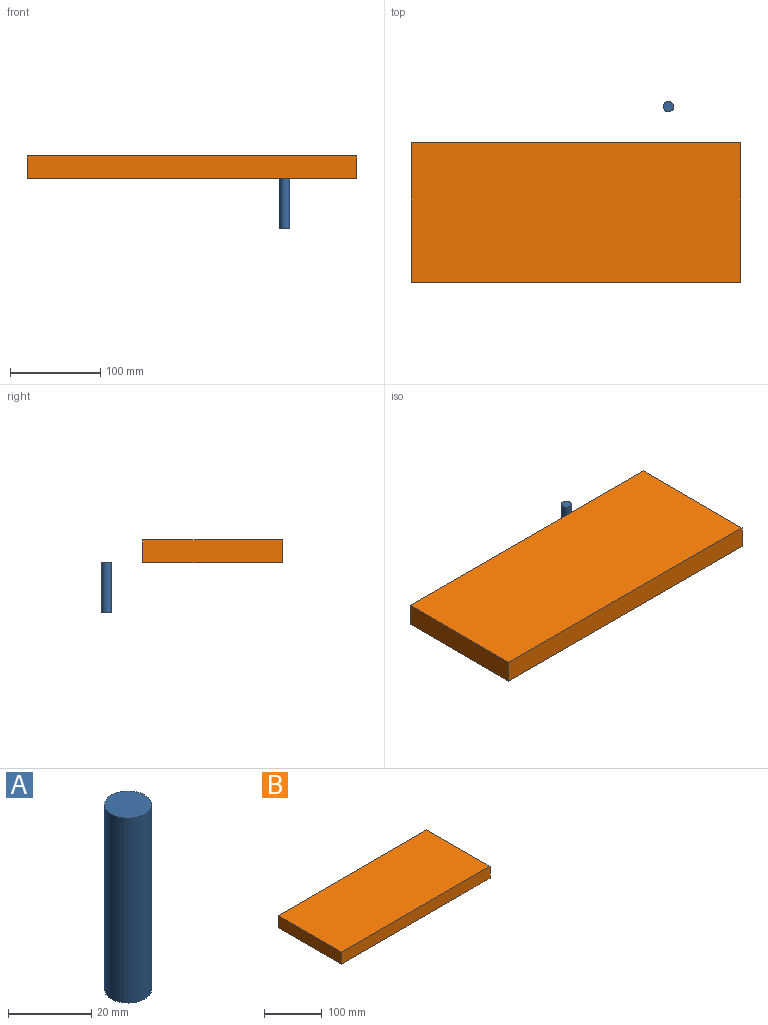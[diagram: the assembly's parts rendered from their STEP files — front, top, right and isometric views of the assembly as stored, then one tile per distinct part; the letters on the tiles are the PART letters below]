
ASSEMBLY  parts=2 mates=1
PART A: 3 faces, bbox 11.3x11.3x54.4 mm
  f0: cylinder r=5.66mm len=54.36mm, axis (0,0,-1), area 1934.7mm2, adj f1,f2
  f1: plane 11.33x11.33mm, normal (0,0,1), area 100.8mm2, adj f0
  f2: plane 11.33x11.33mm, normal (0,0,-1), area 100.8mm2, adj f0
PART B: 6 faces, bbox 364.5x154.8x25.4 mm
  f0: plane 154.82x25.4mm, normal (-1,0,0), area 3932.4mm2, adj f1,f3,f4,f5
  f1: plane 364.45x25.4mm, normal (0,-1,0), area 9257.1mm2, adj f0,f2,f4,f5
  f2: plane 154.82x25.4mm, normal (1,0,0), area 3932.4mm2, adj f1,f3,f4,f5
  f3: plane 364.45x25.4mm, normal (0,1,0), area 9257.1mm2, adj f0,f2,f4,f5
  f4: plane 364.45x154.82mm, normal (0,0,1), area 56423.8mm2, adj f0,f1,f2,f3
  f5: plane 364.45x154.82mm, normal (0,0,-1), area 56423.8mm2, adj f0,f1,f2,f3
PLACE A t=(4.05,-2.75,0.04)mm
PLACE B rot(axis=(0,-1,0),180deg) t=(8.37,-76.23,79.79)mm
MATE planar B.f4 <-> A.f0  axis (0,0,-1) through (-98.28,-120.14,54.39)mm
